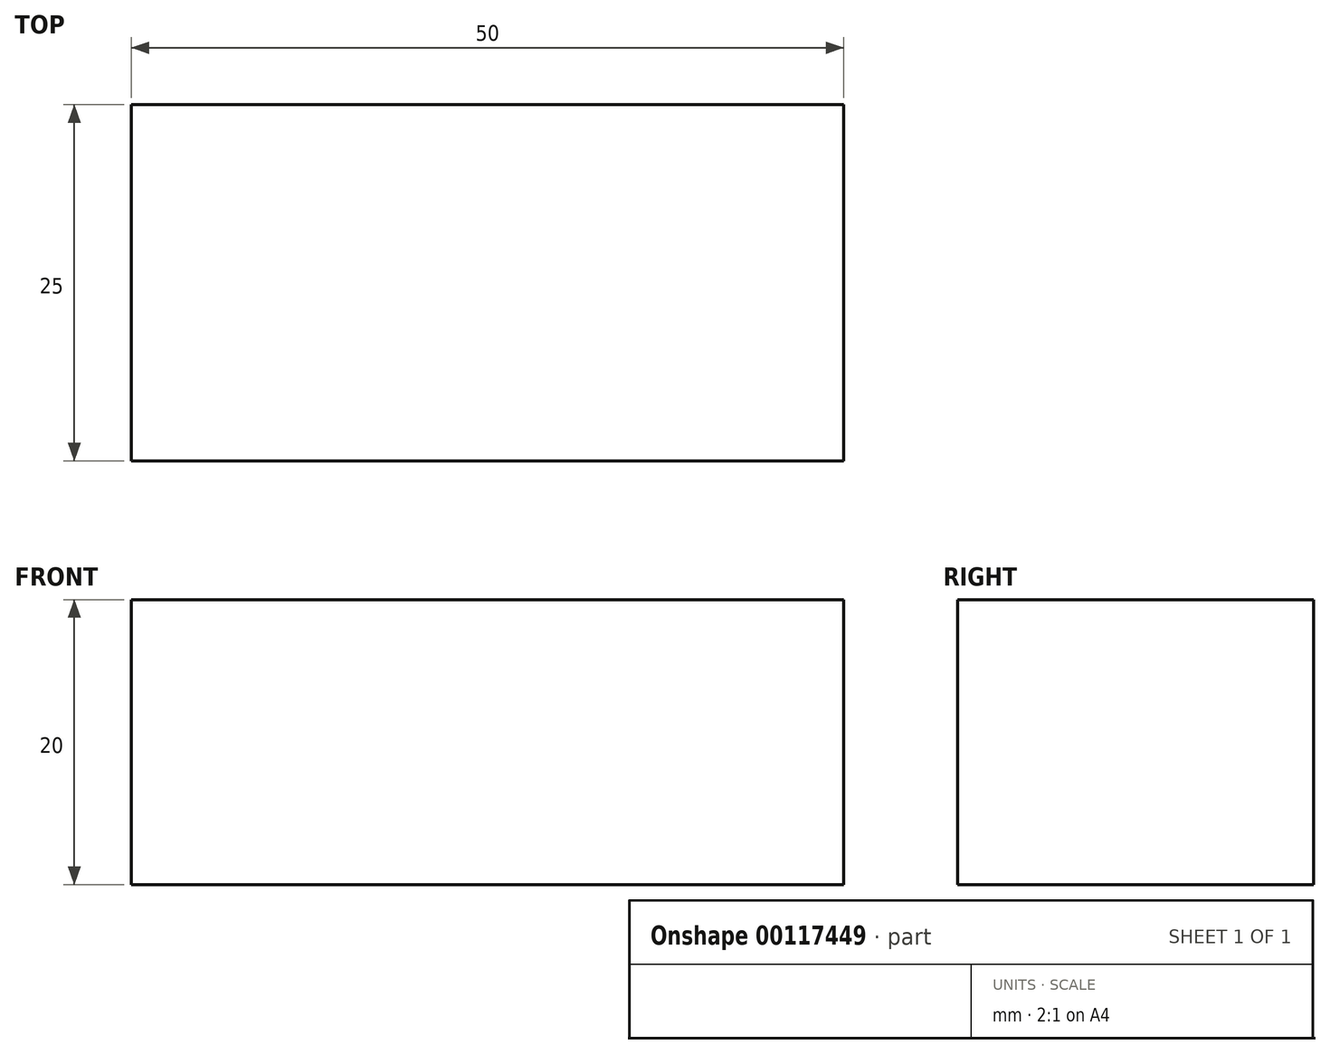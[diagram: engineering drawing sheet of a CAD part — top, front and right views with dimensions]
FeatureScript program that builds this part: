
annotation { "Feature Type Name" : "Feature", "Feature Type Description" : "" }
export const myFeature = defineFeature(function(context is Context, id is Id, definition is map)
    precondition{}
    {
        {
            var Q0;
            Q0=qCreatedBy(makeId("Front.planeOp"),FACE);
            var sketch = newSketch(context, id + "F0", { "sketchPlane" : qUnion([Q0])});
            skLineSegment(sketch, "E0.bottom", {"start": v(-25, 10) * mm, "end": v(25, 10) * mm});
            skLineSegment(sketch, "E0.top", {"start": v(-25, -10) * mm, "end": v(25, -10) * mm});
            skLineSegment(sketch, "E0.left", {"start": v(-25, 10) * mm, "end": v(-25, -10) * mm});
            skLineSegment(sketch, "E0.right", {"start": v(25, 10) * mm, "end": v(25, -10) * mm});
            skPoint(sketch, "E0.middle", {"position": v(0, 0) * mm});
            skSolve(sketch);
        }
        {
            var Q0;
            Q0=makeQuery(id+"F0.imprint","IMPRINT",FACE,{"disambiguationData":[TD([[makeQuery(id+"F0.imprint","IMPRINT",EDGE,{"derivedFrom":sQuery(id+"F0.wireOp",EDGE,"E0.bottom")}),-1.0]])]});
            extrude(context, id + "F1", {"entities" : qUnion([Q0]), "endBound" : BoundingType.SYMMETRIC, "depth" : 25 * mm});
        }
    });
